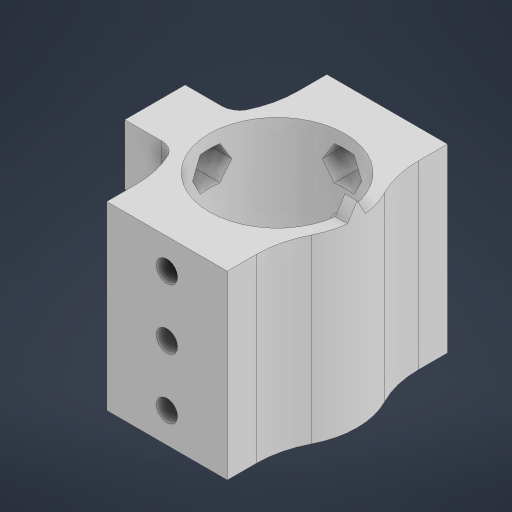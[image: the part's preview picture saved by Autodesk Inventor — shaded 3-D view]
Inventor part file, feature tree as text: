
AUTODESK INVENTOR PART (.ipt)
format: ipt  version: 2023 (Build 270158000, 158)  size: 346,624 bytes
history: native  units: mm
features: extrude x9, sketch x8, plane x2, fillet x2, projected_geometry x1
ambient origin geometry x8: Origin, YZ Plane, XZ Plane, XY Plane, X Axis, Y Axis, Z Axis, Center Point
bodies: Solid1 (feature_tree)
feature tree (22):
  extrude  "Extrusion1"  Depth=2.0mm
  plane  "Work Plane1"
  sketch  "Sketch2"  dims[d2=10.0mm d3=0.0mm d4=15.5mm]
  extrude  "Extrusion3"  Depth=10.0mm
  plane  "Work Plane2"
  extrude  "Extrusion4"  TaperAngle=60.0deg  [1 undecoded]
  sketch  "Sketch7"  dims[d12=12.25mm d13=0.0mm d14=-20.25mm d16=0.2mm]
  extrude  "Extrusion5"  TaperAngle=60.0deg  [1 undecoded]
  extrude  "Extrusion6"  [1 undecoded]
  fillet  "Fillet1"  Radius=0.2mm
  sketch  "Sketch8"  dims[d18=10.25mm d19=0.0mm d20=6.5mm]
  extrude  "Extrusion7"  Depth=6.5mm
  extrude  "Extrusion8"  Depth=10.0mm
  fillet  "Fillet2"  Radius=10.0mm
  extrude  "Extrusion9"  Depth=31.5mm
  extrude  "Extrusion10"  Depth=31.5mm
  sketch  "Sketch1"  dims[d0=22.5mm d1=2.0mm]
  projected_geometry  "Projected Loop1"
  sketch  "Sketch3"  dims[d5=60.0deg d7=60.0deg]
  sketch  "Sketch5"  dims[d8=3.0mm d11=60.0deg]
  sketch  "Sketch9"  dims[d21=60.0mm d23=360.0deg d25=3.6mm d26=10.0mm d27=0.0mm]
  sketch  "Sketch10"  dims[d28=5.0mm d29=0.0mm d30=3.0mm d33=20.0mm d34=5.0mm d35=20.0mm d36=0.0mm d37=9.75mm d38=0.0mm d39=16.0mm d40=3.5mm d41=10.0mm d42=54.5mm d43=0.0mm d44=6.5mm d45=60.0mm d47=360.0deg d49=60.0mm d51=360.0deg d53=60.0mm d55=360.0deg d57=31.5mm d58=0.0mm d31=0.5mm d32=0.872665mm]
note: 3 required parameter values undecoded (feature->parameter linkage not recoverable at this tier; creation-order binding heuristic only, values carry confidence <= 0.55)
